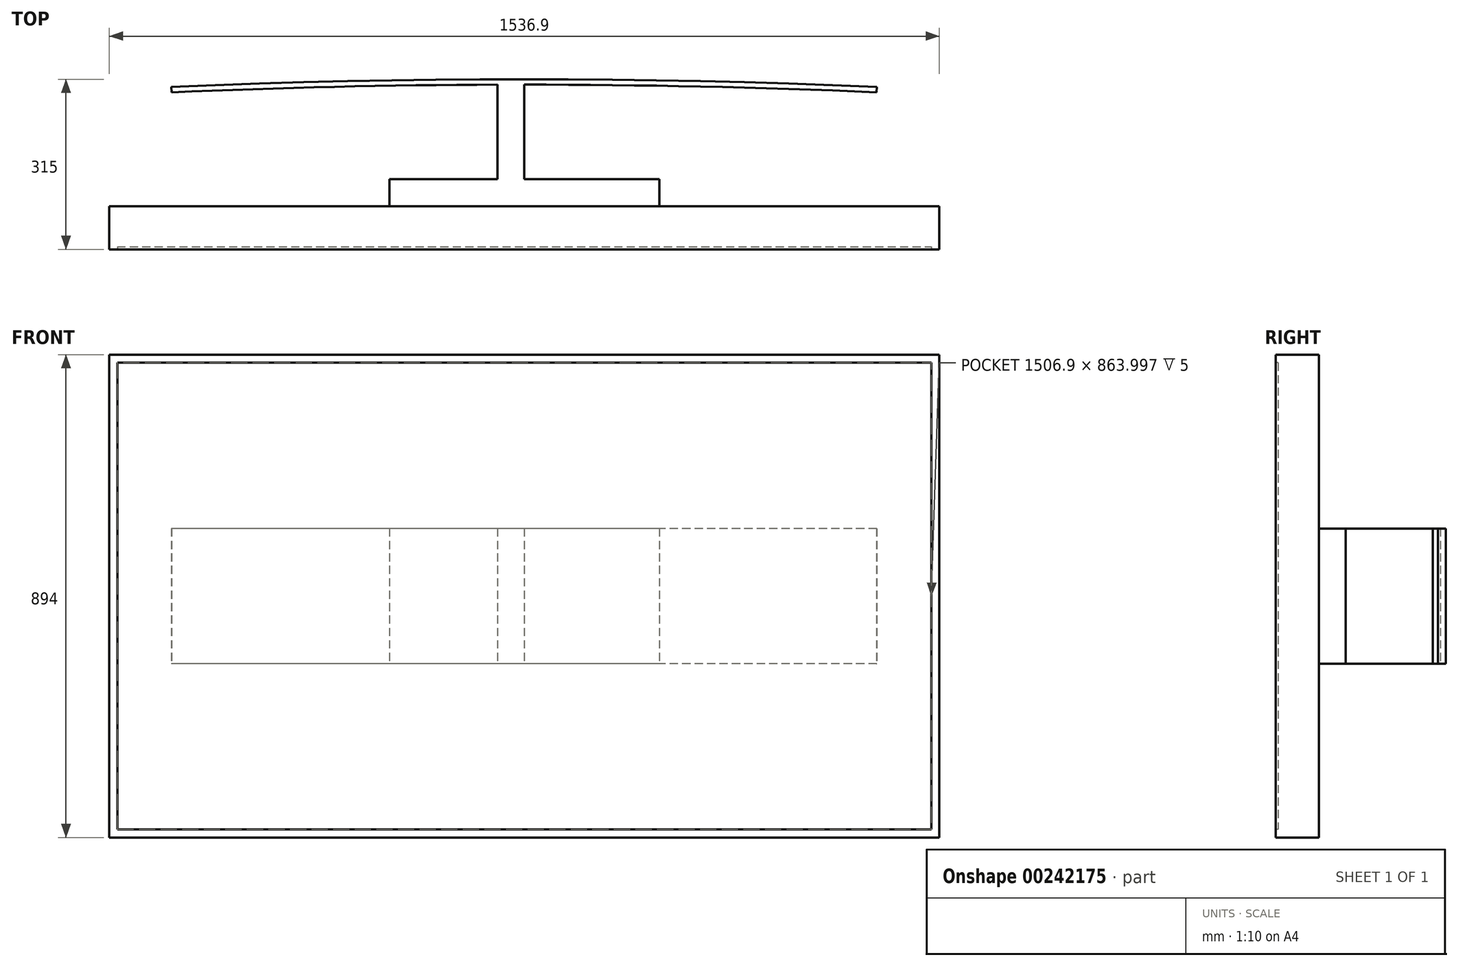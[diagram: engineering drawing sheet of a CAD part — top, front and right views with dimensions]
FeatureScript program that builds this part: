
annotation { "Feature Type Name" : "Feature", "Feature Type Description" : "" }
export const myFeature = defineFeature(function(context is Context, id is Id, definition is map)
    precondition{}
    {
        {
            var Q0;
            Q0=qCreatedBy(makeId("Top.planeOp"),FACE);
            var sketch = newSketch(context, id + "F0", { "sketchPlane" : qUnion([Q0])});
            skCircle(sketch, "E0", {"center": v(0, 0) * mm, "radius": 15000 * mm});
            skCircle(sketch, "E1.0", {"center": v(0, 0) * mm, "radius": 14975 * mm});
            skLineSegment(sketch, "E2", {"start": v(0, 0) * mm, "end": v(0, 14975) * mm});
            skLineSegment(sketch, "E3", {"start": v(0, 0) * mm, "end": v(1305.16, 14918.02) * mm});
            skCircle(sketch, "E4.0", {"center": v(0, 0) * mm, "radius": 14985 * mm});
            skLineSegment(sketch, "E5", {"start": v(0, 0) * mm, "end": v(652.58, 14970.78) * mm});
            skPoint(sketch, "E5.endSnap0", {"position": v(652.58, 7459) * mm});
            skLineSegment(sketch, "E6", {"start": v(0, 0) * mm, "end": v(-654.3, 14985.72) * mm});
            skLineSegment(sketch, "E7.bottom", {"start": v(250, 14750) * mm, "end": v(-250, 14750) * mm});
            skLineSegment(sketch, "E7.top", {"start": v(250, 14800) * mm, "end": v(-250, 14800) * mm});
            skLineSegment(sketch, "E7.left", {"start": v(250, 14750) * mm, "end": v(250, 14800) * mm});
            skLineSegment(sketch, "E7.right", {"start": v(-250, 14750) * mm, "end": v(-250, 14800) * mm});
            skPoint(sketch, "E7.middle", {"position": v(0, 14775) * mm});
            skLineSegment(sketch, "E8.0", {"start": v(50, 0) * mm, "end": v(50, 14974.92) * mm});
            skLineSegment(sketch, "E9.0", {"start": v(-50, 0) * mm, "end": v(-50, 14974.92) * mm});
            skSolve(sketch);
        }
        {
            var Q0;
            {var subQ0=sQuery(id+"F0.wireOp",EDGE,"E1.0");var subQ5=makeQuery(id+"F0.imprint","INTERSECT",VERTEX,{"derivedFrom":[subQ0,sQuery(id+"F0.wireOp",EDGE,"E9.0")]});Q0=makeQuery(id+"F0.imprint","IMPRINT",FACE,{"disambiguationData":[TD([[makeQuery(id+"F0.imprint","IMPRINT",EDGE,{"disambiguationData":[TD([[subQ5,1.0]])],"derivedFrom":subQ0}),1.0]])]});}
            var Q1;
            {var subQ0=sQuery(id+"F0.wireOp",EDGE,"E2");var subQ1=sQuery(id+"F0.wireOp",EDGE,"E1.0");var subQ2=makeQuery(id+"F0.imprint","INTERSECT",VERTEX,{"derivedFrom":[subQ1,subQ0]});Q1=makeQuery(id+"F0.imprint","IMPRINT",FACE,{"disambiguationData":[TD([[makeQuery(id+"F0.imprint","IMPRINT",EDGE,{"disambiguationData":[TD([[subQ2,1.0]])],"derivedFrom":subQ1}),-1.0]])]});}
            var Q2;
            {var subQ0=sQuery(id+"F0.wireOp",EDGE,"E2");var subQ1=sQuery(id+"F0.wireOp",EDGE,"E1.0");var subQ2=makeQuery(id+"F0.imprint","INTERSECT",VERTEX,{"derivedFrom":[subQ1,subQ0]});Q2=makeQuery(id+"F0.imprint","IMPRINT",FACE,{"disambiguationData":[TD([[makeQuery(id+"F0.imprint","IMPRINT",EDGE,{"disambiguationData":[TD([[subQ2,-1.0]])],"derivedFrom":subQ1}),-1.0]])]});}
            var Q3;
            {var subQ0=sQuery(id+"F0.wireOp",EDGE,"E7.right");Q3=makeQuery(id+"F0.imprint","IMPRINT",FACE,{"disambiguationData":[TD([[makeQuery(id+"F0.imprint","IMPRINT",EDGE,{"derivedFrom":subQ0}),-1.0]])]});}
            var Q4;
            {var subQ0=sQuery(id+"F0.wireOp",EDGE,"E7.bottom");var subQ1=sQuery(id+"F0.wireOp",EDGE,"E2");var subQ2=makeQuery(id+"F0.imprint","INTERSECT",VERTEX,{"derivedFrom":[subQ1,subQ0]});Q4=makeQuery(id+"F0.imprint","IMPRINT",FACE,{"disambiguationData":[TD([[makeQuery(id+"F0.imprint","IMPRINT",EDGE,{"disambiguationData":[TD([[subQ2,-1.0]])],"derivedFrom":subQ1}),1.0]])]});}
            var Q5;
            {var subQ0=sQuery(id+"F0.wireOp",EDGE,"E7.bottom");var subQ1=sQuery(id+"F0.wireOp",EDGE,"E2");var subQ2=makeQuery(id+"F0.imprint","INTERSECT",VERTEX,{"derivedFrom":[subQ1,subQ0]});Q5=makeQuery(id+"F0.imprint","IMPRINT",FACE,{"disambiguationData":[TD([[makeQuery(id+"F0.imprint","IMPRINT",EDGE,{"disambiguationData":[TD([[subQ2,-1.0]])],"derivedFrom":subQ1}),-1.0]])]});}
            var Q6;
            {var subQ0=sQuery(id+"F0.wireOp",EDGE,"E7.left");Q6=makeQuery(id+"F0.imprint","IMPRINT",FACE,{"disambiguationData":[TD([[makeQuery(id+"F0.imprint","IMPRINT",EDGE,{"derivedFrom":subQ0}),1.0]])]});}
            extrude(context, id + "F1", {"entities" : qUnion([Q0, Q1, Q2, Q3, Q4, Q5, Q6]), "depth" : 250 * mm});
        }
        {
            var Q0;
            Q0=makeQuery(id+"F1.opExtrude","SWEPT_FACE",FACE,{"disambiguationData":[OSD([sQuery(id+"F0.wireOp",EDGE,"E7.bottom")])]});
            var sketch = newSketch(context, id + "F2", { "sketchPlane" : qUnion([Q0])});
            skLineSegment(sketch, "E10", {"start": v(0, 250) * mm, "end": v(0, 0) * mm});
            skLineSegment(sketch, "E11.bottom", {"start": v(768.45, 572) * mm, "end": v(-768.45, 572) * mm});
            skLineSegment(sketch, "E11.top", {"start": v(768.45, -322) * mm, "end": v(-768.45, -322) * mm});
            skLineSegment(sketch, "E11.left", {"start": v(768.45, 572) * mm, "end": v(768.45, -322) * mm});
            skLineSegment(sketch, "E11.right", {"start": v(-768.45, 572) * mm, "end": v(-768.45, -322) * mm});
            skPoint(sketch, "E11.middle", {"position": v(0, 125) * mm});
            skSolve(sketch);
        }
        {
            var Q0;
            Q0 = qSketchRegion(id + "F2", true);
            extrude(context, id + "F3", {"entities" : qUnion([Q0]), "operationType" : NewBodyOperationType.ADD, "depth" : 80 * mm});
        }
        {
            var Q0;
            Q0=makeQuery(id+"F3.opExtrude","CAP_FACE",FACE,{"disambiguationData":[OSD([sQuery(id+"F2.wireOp",EDGE,"E11.bottom"),sQuery(id+"F2.wireOp",EDGE,"E11.top"),sQuery(id+"F2.wireOp",EDGE,"E11.left"),sQuery(id+"F2.wireOp",EDGE,"E11.right")])],"isStart":false});
            var sketch = newSketch(context, id + "F4", { "sketchPlane" : qUnion([Q0])});
            skLineSegment(sketch, "E12.0", {"start": v(-753.45, -307) * mm, "end": v(753.45, -307) * mm});
            skLineSegment(sketch, "E12.1", {"start": v(-753.45, 557) * mm, "end": v(-753.45, -307) * mm});
            skLineSegment(sketch, "E12.2", {"start": v(753.45, 557) * mm, "end": v(-753.45, 557) * mm});
            skLineSegment(sketch, "E12.3", {"start": v(753.45, -307) * mm, "end": v(753.45, 557) * mm});
            skSolve(sketch);
        }
        {
            var Q0;
            Q0 = qSketchRegion(id + "F4", true);
            extrude(context, id + "F5", {"entities" : qUnion([Q0]), "operationType" : NewBodyOperationType.REMOVE, "oppositeDirection" : true, "depth" : 5 * mm});
        }
    });
